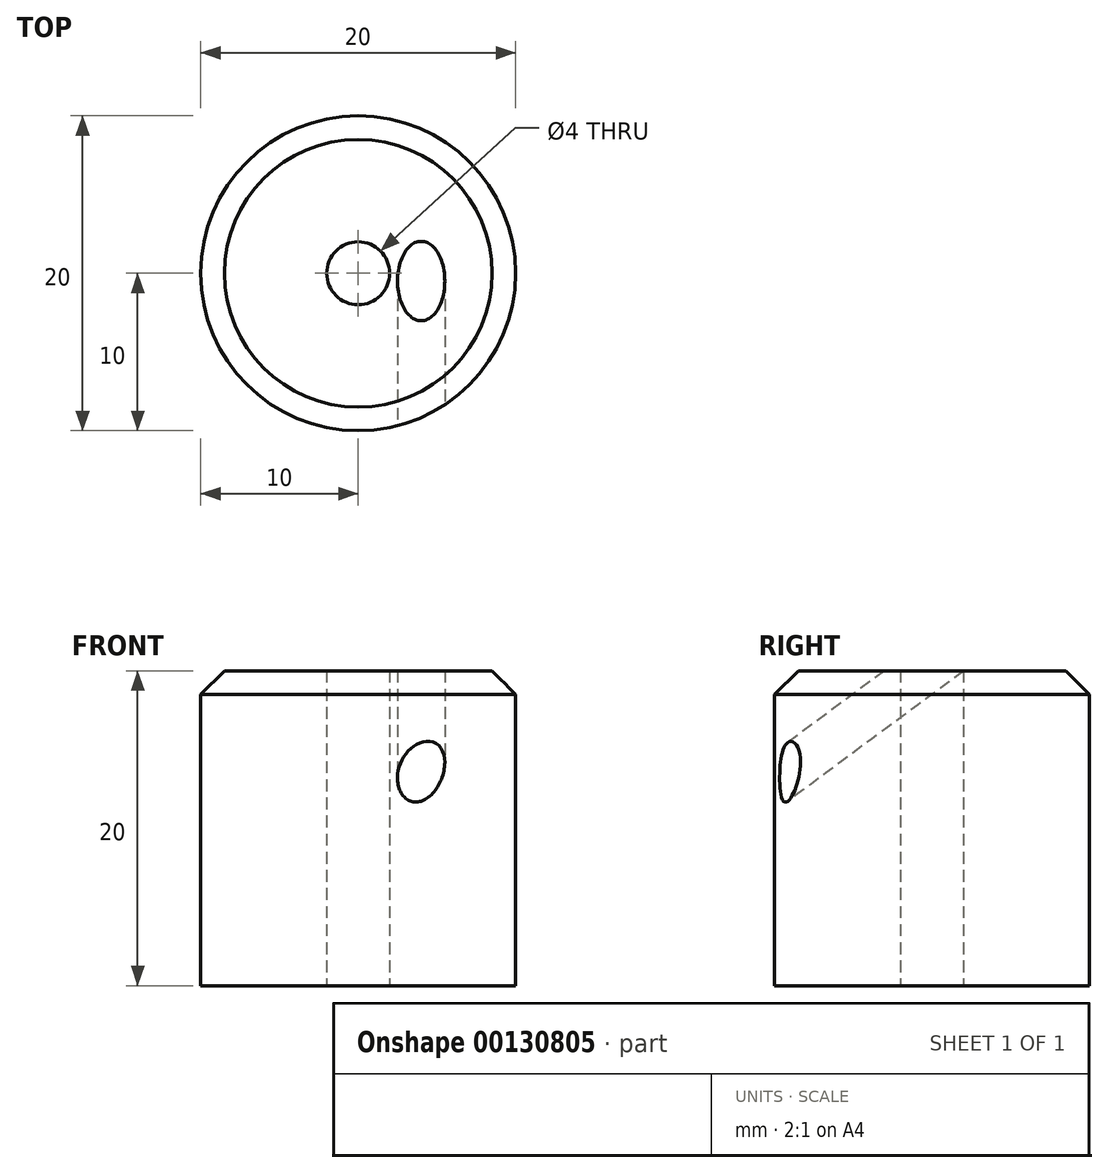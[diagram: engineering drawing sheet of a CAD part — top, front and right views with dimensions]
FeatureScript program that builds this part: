
annotation { "Feature Type Name" : "Feature", "Feature Type Description" : "" }
export const myFeature = defineFeature(function(context is Context, id is Id, definition is map)
    precondition{}
    {
        {
            var Q0;
            Q0=qCreatedBy(makeId("Top.planeOp"),FACE);
            var sketch = newSketch(context, id + "F0", { "sketchPlane" : qUnion([Q0])});
            skCircle(sketch, "E0", {"center": v(0, 0) * mm, "radius": 10 * mm});
            skCircle(sketch, "E1", {"center": v(0, 0) * mm, "radius": 2 * mm});
            skSolve(sketch);
        }
        {
            var Q0;
            Q0=makeQuery(id+"F0.imprint","IMPRINT",FACE,{"disambiguationData":[TD([[makeQuery(id+"F0.imprint","IMPRINT",EDGE,{"derivedFrom":sQuery(id+"F0.wireOp",EDGE,"E0")}),1.0]])]});
            extrude(context, id + "F1", {"entities" : qUnion([Q0]), "depth" : 20 * mm});
        }
        {
            var Q0;
            Q0=qCreatedBy(makeId("Right.planeOp"),FACE);
            cPlane(context, id + "F2", {"entities" : qUnion([Q0]), "cplaneType" : CPlaneType.OFFSET, "offset" : 4 * mm, "width" : 150 * mm, "height" : 150 * mm});
        }
        {
            var Q0;
            Q0=qCreatedBy(id+"F2.planeOp",FACE);
            var sketch = newSketch(context, id + "F3", { "sketchPlane" : qUnion([Q0])});
            skLineSegment(sketch, "E2", {"start": v(3.48, 22.94) * mm, "end": v(-17.47, 7.44) * mm});
            skSolve(sketch);
        }
        {
            var Q0;
            Q0=sQuery(id+"F3.wireOp",VERTEX,"E2.start");
            var Q1;
            Q1=sQuery(id+"F3.wireOp",EDGE,"E2");
            cPlane(context, id + "F4", {"entities" : qUnion([Q0, Q1]), "cplaneType" : CPlaneType.LINE_POINT, "offset" : 25 * mm, "width" : 150 * mm, "height" : 150 * mm});
        }
        {
            var Q0;
            Q0=qCreatedBy(id+"F4.planeOp",FACE);
            var sketch = newSketch(context, id + "F5", { "sketchPlane" : qUnion([Q0])});
            skCircle(sketch, "E3", {"center": v(4, 16.37) * mm, "radius": 1.5 * mm});
            skSolve(sketch);
        }
        {
            var Q0;
            Q0=makeQuery(id+"F5.imprint","IMPRINT",FACE,{"disambiguationData":[TD([[makeQuery(id+"F5.imprint","IMPRINT",EDGE,{"derivedFrom":sQuery(id+"F5.wireOp",EDGE,"E3")}),1.0]])]});
            var Q1;
            Q1=sQuery(id+"F3.wireOp",EDGE,"E2");
            sweep(context, id + "F6", {"operationType" : NewBodyOperationType.REMOVE, "profiles" : qUnion([Q0]), "path" : qUnion([Q1])});
        }
        {
            var Q0;
            Q0=makeQuery(id+"F1.opExtrude","CAP_EDGE",EDGE,{"disambiguationData":[OSD([sQuery(id+"F0.wireOp",EDGE,"E0")])],"isStart":false});
            chamfer(context, id + "F7", {"entities" : qUnion([Q0]), "width" : 1.5 * mm, "tangentPropagation" : true});
        }
    });
